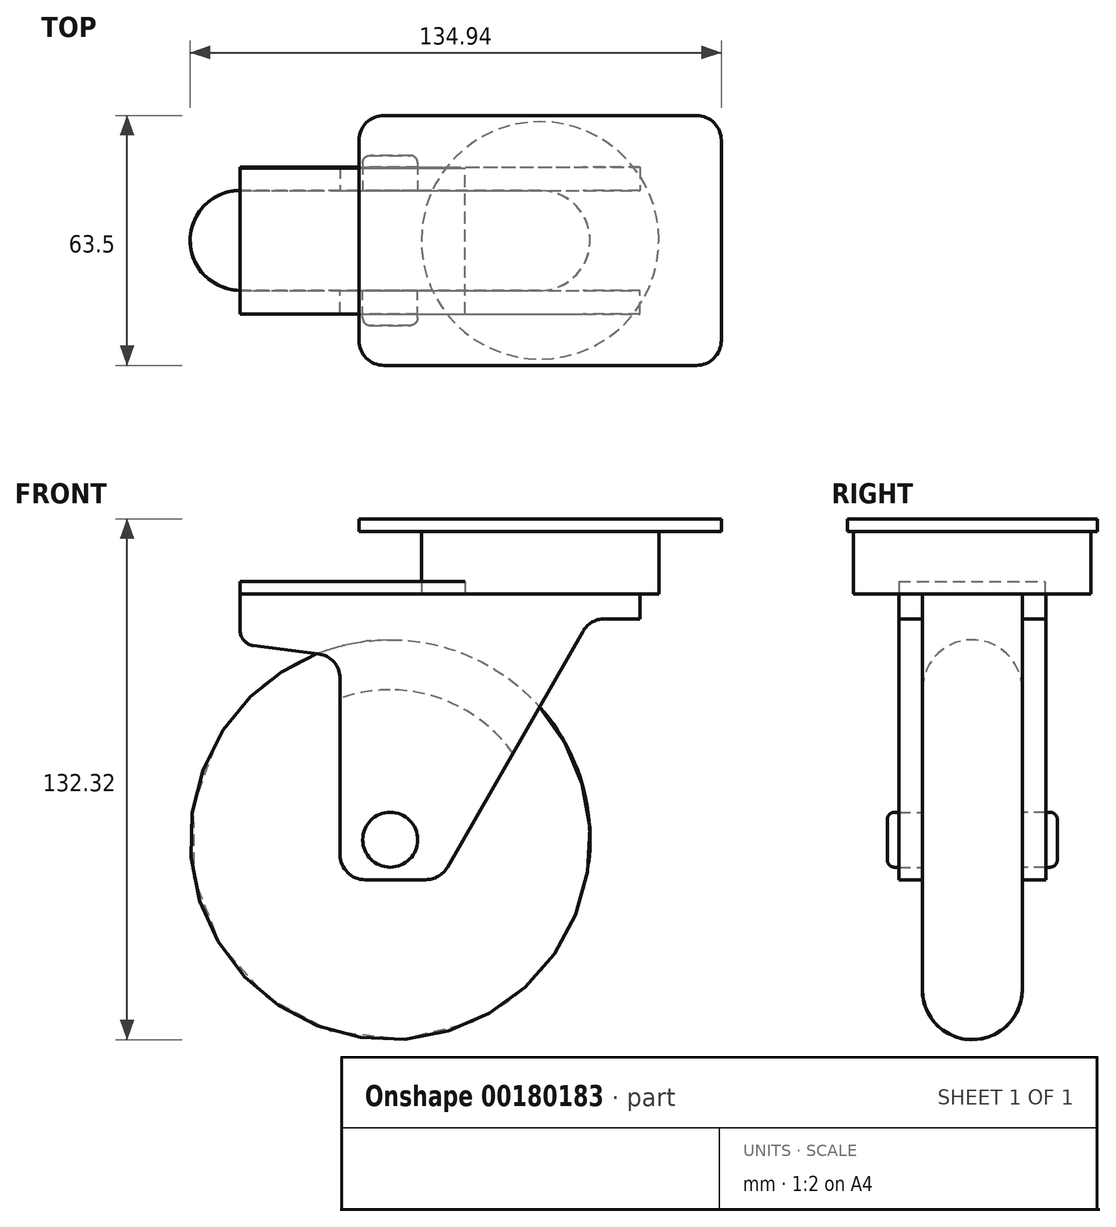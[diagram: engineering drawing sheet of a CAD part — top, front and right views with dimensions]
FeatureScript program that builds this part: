
annotation { "Feature Type Name" : "Feature", "Feature Type Description" : "" }
export const myFeature = defineFeature(function(context is Context, id is Id, definition is map)
    precondition{}
    {
        {
            var Q0;
            Q0=qCreatedBy(makeId("Right.planeOp"),FACE);
            var sketch = newSketch(context, id + "F0", { "sketchPlane" : qUnion([Q0])});
            skLineSegment(sketch, "E0.bottom", {"start": v(0, 0) * mm, "end": v(12.7, 0) * mm});
            skLineSegment(sketch, "E0.top", {"start": v(0, 50.8) * mm, "end": v(0, 50.8) * mm});
            skLineSegment(sketch, "E0.left", {"start": v(0, 0) * mm, "end": v(0, 50.8) * mm});
            skLineSegment(sketch, "E0.right", {"start": v(12.7, 0) * mm, "end": v(12.7, 38.1) * mm});
            skPoint(sketch, "E1.visualSharp", {"position": v(12.7, 50.8) * mm});
            skArc(sketch, "E1.filletArc", {"start": v(12.7, 38.1) * mm, "mid": v(8.98, 47.08) * mm, "end": v(0, 50.8) * mm});
            skLineSegment(sketch, "E2", {"start": v(0, 0) * mm, "end": v(29.52, 0) * mm, "construction": true});
            skPoint(sketch, "E2.endSnap0", {"position": v(6.35, 0) * mm});
            skLineSegment(sketch, "E3.MirrorCS", {"start": v(0, 0) * mm, "end": v(-12.7, 0) * mm});
            skLineSegment(sketch, "E4.MirrorCS", {"start": v(-12.7, 0) * mm, "end": v(-12.7, 38.1) * mm});
            skArc(sketch, "E5.MirrorCS", {"start": v(-12.7, 38.1) * mm, "mid": v(-8.98, 47.08) * mm, "end": v(0, 50.8) * mm});
            skLineSegment(sketch, "E6.MirrorCS", {"start": v(0, 0) * mm, "end": v(-29.52, 0) * mm, "construction": true});
            skSolve(sketch);
        }
        {
            var Q0;
            Q0=makeQuery(id+"F0.imprint","IMPRINT",FACE,{"disambiguationData":[TD([[makeQuery(id+"F0.imprint","IMPRINT",EDGE,{"derivedFrom":sQuery(id+"F0.wireOp",EDGE,"E0.left")}),1.0]])]});
            var Q1;
            Q1=makeQuery(id+"F0.imprint","IMPRINT",FACE,{"disambiguationData":[TD([[makeQuery(id+"F0.imprint","IMPRINT",EDGE,{"derivedFrom":sQuery(id+"F0.wireOp",EDGE,"E0.bottom")}),1.0]])]});
            var Q2;
            Q2=sQuery(id+"F0.wireOp",EDGE,"E6.MirrorCS");
            revolve(context, id + "F1", {"entities" : qUnion([Q0, Q1]), "axis" : qUnion([Q2]), "revolveType" : RevolveType.FULL});
        }
        {
            var Q0;
            Q0=makeQuery(id+"F1.opRevolve","SWEPT_FACE",FACE,{"disambiguationData":[OSD([sQuery(id+"F0.wireOp",EDGE,"E4.MirrorCS")])]});
            var sketch = newSketch(context, id + "F2", { "sketchPlane" : qUnion([Q0])});
            skCircle(sketch, "E7", {"center": v(0, 0) * mm, "radius": 6.99 * mm});
            skSolve(sketch);
        }
        {
            var Q0;
            Q0=qSketchRegion(id+"F2",true);
            extrude(context, id + "F3", {"entities" : qUnion([Q0]), "operationType" : NewBodyOperationType.ADD, "depth" : 8.9 * mm});
        }
        {
            var Q0;
            Q0=makeQuery(id+"F3.opExtrude","CAP_EDGE",EDGE,{"disambiguationData":[OSD([sQuery(id+"F2.wireOp",EDGE,"E7")])],"isStart":false});
            fillet(context, id + "F4", {"entities" : qUnion([Q0]), "radius" : 1.96 * mm, "tangentPropagation" : true, "allowEdgeOverflow" : false});
        }
        {
            var Q0;
            Q0=makeQuery(id+"F1.opRevolve","SWEPT_FACE",FACE,{"disambiguationData":[OSD([sQuery(id+"F0.wireOp",EDGE,"E0.right")])]});
            var sketch = newSketch(context, id + "F5", { "sketchPlane" : qUnion([Q0])});
            skCircle(sketch, "E8", {"center": v(0, 0) * mm, "radius": 6.99 * mm});
            skSolve(sketch);
        }
        {
            var Q0;
            Q0=qSketchRegion(id+"F5",true);
            extrude(context, id + "F6", {"entities" : qUnion([Q0]), "operationType" : NewBodyOperationType.ADD, "depth" : 8.9 * mm});
        }
        {
            var Q0;
            Q0=makeQuery(id+"F6.opExtrude","CAP_FACE",FACE,{"disambiguationData":[OSD([sQuery(id+"F5.wireOp",EDGE,"E8")])],"isStart":false});
            fillet(context, id + "F7", {"entities" : qUnion([Q0]), "radius" : 1.84 * mm, "tangentPropagation" : true, "allowEdgeOverflow" : false});
        }
        {
            var Q0;
            Q0=makeQuery(id+"F1.opRevolve","SWEPT_FACE",FACE,{"disambiguationData":[OSD([sQuery(id+"F0.wireOp",EDGE,"E4.MirrorCS")])]});
            var sketch = newSketch(context, id + "F8", { "sketchPlane" : qUnion([Q0])});
            skLineSegment(sketch, "E9.top", {"start": v(0, 62.47) * mm, "end": v(12.7, 62.47) * mm});
            skLineSegment(sketch, "E9.left", {"start": v(0, 0) * mm, "end": v(0, 62.47) * mm, "construction": true});
            skLineSegment(sketch, "E9.right", {"start": v(12.7, 0) * mm, "end": v(12.7, 62.47) * mm});
            skLineSegment(sketch, "E10.top", {"start": v(1.75, 62.47) * mm, "end": v(-12.7, 62.47) * mm});
            skLineSegment(sketch, "E10.right", {"start": v(-12.7, 0) * mm, "end": v(-12.7, 40.93) * mm});
            skLineSegment(sketch, "E11.top", {"start": v(-6.35, -10.16) * mm, "end": v(9.03, -10.16) * mm});
            skLineSegment(sketch, "E11.left", {"start": v(-12.7, 0) * mm, "end": v(-12.7, -3.81) * mm});
            skLineSegment(sketch, "E11.right", {"start": v(12.7, 0) * mm, "end": v(12.7, -10.16) * mm});
            skPoint(sketch, "E12.visualSharp", {"position": v(-12.7, -10.16) * mm});
            skArc(sketch, "E12.filletArc", {"start": v(-12.7, -3.81) * mm, "mid": v(-10.84, -8.3) * mm, "end": v(-6.35, -10.16) * mm});
            skLineSegment(sketch, "E13", {"start": v(0, 62.47) * mm, "end": v(-38.1, 62.47) * mm});
            skLineSegment(sketch, "E14", {"start": v(-38.1, 62.47) * mm, "end": v(-38.1, 53.12) * mm});
            skLineSegment(sketch, "E15", {"start": v(-34.77, 49.34) * mm, "end": v(-18.24, 47.23) * mm});
            skLineSegment(sketch, "E16", {"start": v(12.7, 62.47) * mm, "end": v(63.5, 62.47) * mm});
            skLineSegment(sketch, "E17", {"start": v(63.5, 62.47) * mm, "end": v(63.5, 56.12) * mm});
            skLineSegment(sketch, "E18", {"start": v(63.5, 56.12) * mm, "end": v(54.47, 56.12) * mm});
            skLineSegment(sketch, "E19", {"start": v(14.53, -6.97) * mm, "end": v(48.97, 52.94) * mm});
            skPoint(sketch, "E20.visualSharp", {"position": v(12.7, -10.16) * mm});
            skArc(sketch, "E20.filletArc", {"start": v(9.03, -10.16) * mm, "mid": v(12.2, -9.3) * mm, "end": v(14.53, -6.97) * mm});
            skArc(sketch, "E21.filletArc", {"start": v(-12.7, 40.93) * mm, "mid": v(-14.28, 45.13) * mm, "end": v(-18.24, 47.23) * mm});
            skPoint(sketch, "E22.visualSharp", {"position": v(-38.1, 49.77) * mm});
            skArc(sketch, "E22.filletArc", {"start": v(-38.1, 53.12) * mm, "mid": v(-37.15, 50.6) * mm, "end": v(-34.77, 49.34) * mm});
            skPoint(sketch, "E23.visualSharp", {"position": v(50.8, 56.12) * mm});
            skArc(sketch, "E23.filletArc", {"start": v(54.47, 56.12) * mm, "mid": v(51.3, 55.27) * mm, "end": v(48.97, 52.94) * mm});
            skSolve(sketch);
        }
        {
            var Q0;
            Q0=qSketchRegion(id+"F8",true);
            extrude(context, id + "F9", {"entities" : qUnion([Q0]), "operationType" : NewBodyOperationType.ADD, "depth" : 5.97 * mm});
        }
        {
            var Q0;
            Q0=makeQuery(id+"F1.opRevolve","SWEPT_BODY",BODY,{"disambiguationData":[OSD([sQuery(id+"F0.wireOp",EDGE,"E0.bottom"),sQuery(id+"F0.wireOp",EDGE,"E0.right"),sQuery(id+"F0.wireOp",EDGE,"E1.filletArc"),sQuery(id+"F0.wireOp",EDGE,"E3.MirrorCS"),sQuery(id+"F0.wireOp",EDGE,"E4.MirrorCS"),sQuery(id+"F0.wireOp",EDGE,"E5.MirrorCS")])]});
            var Q1;
            Q1=qCreatedBy(makeId("Front.planeOp"),FACE);
            mirror(context, id + "F10", {"entities" : qUnion([Q0]), "mirrorPlane" : qUnion([Q1])});
        }
        {
            var Q0;
            Q0=makeQuery(id+"F9.opExtrude","SWEPT_FACE",FACE,{"disambiguationData":[OSD([sQuery(id+"F8.wireOp",EDGE,"E9.top"),sQuery(id+"F8.wireOp",EDGE,"E10.top"),sQuery(id+"F8.wireOp",EDGE,"E13"),sQuery(id+"F8.wireOp",EDGE,"E16")])]});
            var sketch = newSketch(context, id + "F11", { "sketchPlane" : qUnion([Q0])});
            skLineSegment(sketch, "E24", {"start": v(0, 0) * mm, "end": v(38.1, 0) * mm, "construction": true});
            skCircle(sketch, "E25", {"center": v(38.1, 0) * mm, "radius": 30.16 * mm});
            skSolve(sketch);
        }
        {
            var Q0;
            {var subQ0=sQuery(id+"F11.wireOp",EDGE,"E25");var subQ1=sQuery(id+"F8.wireOp",EDGE,"E16");var subQ4=makeQuery(id+"F9.opExtrude","SWEPT_EDGE",EDGE,{"disambiguationData":[OSD([subQ1,sQuery(id+"F8.wireOp",EDGE,"E17")])]});var subQ5=makeQuery(id+"F11.imprint","INTERSECT",VERTEX,{"derivedFrom":[subQ4,subQ0]});Q0=makeQuery(id+"F11.imprint","IMPRINT",FACE,{"disambiguationData":[TD([[makeQuery(id+"F11.imprint","IMPRINT",EDGE,{"disambiguationData":[TD([[subQ5,-1.0]])],"derivedFrom":subQ0}),1.0]])]});}
            var Q1;
            {var subQ0=sQuery(id+"F8.wireOp",EDGE,"E16");var subQ5=makeQuery(id+"F9.opExtrude","SWEPT_EDGE",EDGE,{"disambiguationData":[OSD([subQ0,sQuery(id+"F8.wireOp",EDGE,"E17")])]});var subQ7=sQuery(id+"F11.wireOp",EDGE,"E25");var subQ9=makeQuery(id+"F11.imprint","INTERSECT",VERTEX,{"derivedFrom":[subQ5,subQ7]});Q1=makeQuery(id+"F11.imprint","IMPRINT",FACE,{"disambiguationData":[TD([[makeQuery(id+"F11.imprint","IMPRINT",EDGE,{"disambiguationData":[TD([[subQ9,1.0]])],"derivedFrom":subQ7}),1.0]])]});}
            var Q2;
            {var subQ0=sQuery(id+"F11.wireOp",EDGE,"E25");var subQ1=makeQuery(id+"F9.opExtrude","CAP_EDGE",EDGE,{"disambiguationData":[OSD([sQuery(id+"F8.wireOp",EDGE,"E9.top"),sQuery(id+"F8.wireOp",EDGE,"E10.top"),sQuery(id+"F8.wireOp",EDGE,"E13"),sQuery(id+"F8.wireOp",EDGE,"E16")])],"isStart":false});var subQ2=makeQuery(id+"F11.imprint","INTERSECT",VERTEX,{"disambiguationData":[OD(0.0)],"derivedFrom":[subQ1,subQ0]});Q2=makeQuery(id+"F11.imprint","IMPRINT",FACE,{"disambiguationData":[TD([[makeQuery(id+"F11.imprint","IMPRINT",EDGE,{"disambiguationData":[TD([[subQ2,-1.0]])],"derivedFrom":subQ0}),1.0]])]});}
            var Q3;
            Q3=sQuery(id+"F11.wireOp",EDGE,"E25");
            extrude(context, id + "F12", {"entities" : qUnion([Q0, Q1, Q2]), "surfaceEntities" : qUnion([Q3]), "depth" : 19.05 * mm});
        }
        {
            var Q0;
            Q0=makeQuery(id+"F12.opExtrude","CAP_FACE",FACE,{"disambiguationData":[OSD([sQuery(id+"F11.wireOp",EDGE,"E25")])],"isStart":false});
            var sketch = newSketch(context, id + "F13", { "sketchPlane" : qUnion([Q0])});
            skLineSegment(sketch, "E26.bottom", {"start": v(77.79, -31.75) * mm, "end": v(-1.59, -31.75) * mm});
            skLineSegment(sketch, "E26.top", {"start": v(77.79, 31.75) * mm, "end": v(-1.59, 31.75) * mm});
            skLineSegment(sketch, "E26.left", {"start": v(84.14, -25.4) * mm, "end": v(84.14, 25.4) * mm});
            skLineSegment(sketch, "E26.right", {"start": v(-7.94, -25.4) * mm, "end": v(-7.94, 25.4) * mm});
            skPoint(sketch, "E26.middle", {"position": v(38.1, 0) * mm});
            skPoint(sketch, "E27.visualSharp", {"position": v(84.14, 31.75) * mm});
            skArc(sketch, "E27.filletArc", {"start": v(84.14, 25.4) * mm, "mid": v(82.28, 29.9) * mm, "end": v(77.79, 31.75) * mm});
            skPoint(sketch, "E28.visualSharp", {"position": v(84.14, -31.75) * mm});
            skArc(sketch, "E28.filletArc", {"start": v(77.79, -31.75) * mm, "mid": v(82.28, -29.9) * mm, "end": v(84.14, -25.4) * mm});
            skPoint(sketch, "E29.visualSharp", {"position": v(-7.94, -31.75) * mm});
            skArc(sketch, "E29.filletArc", {"start": v(-7.94, -25.4) * mm, "mid": v(-6.08, -29.9) * mm, "end": v(-1.59, -31.75) * mm});
            skPoint(sketch, "E30.visualSharp", {"position": v(-7.94, 31.75) * mm});
            skArc(sketch, "E30.filletArc", {"start": v(-1.59, 31.75) * mm, "mid": v(-6.08, 29.9) * mm, "end": v(-7.94, 25.4) * mm});
            skSolve(sketch);
        }
        {
            var Q0;
            Q0=qSketchRegion(id+"F13",true);
            extrude(context, id + "F14", {"entities" : qUnion([Q0]), "operationType" : NewBodyOperationType.ADD, "oppositeDirection" : true, "depth" : 3.17 * mm});
        }
        {
            var Q0;
            Q0=makeQuery(id+"F9.opExtrude","SWEPT_FACE",FACE,{"disambiguationData":[OSD([sQuery(id+"F8.wireOp",EDGE,"E9.top"),sQuery(id+"F8.wireOp",EDGE,"E10.top"),sQuery(id+"F8.wireOp",EDGE,"E13"),sQuery(id+"F8.wireOp",EDGE,"E16")])]});
            var sketch = newSketch(context, id + "F15", { "sketchPlane" : qUnion([Q0])});
            skLineSegment(sketch, "E31.bottom", {"start": v(-38.1, -18.67) * mm, "end": v(19.05, -18.67) * mm});
            skLineSegment(sketch, "E31.top", {"start": v(-38.1, 18.42) * mm, "end": v(19.05, 18.42) * mm});
            skLineSegment(sketch, "E31.left", {"start": v(-38.1, -18.67) * mm, "end": v(-38.1, 18.42) * mm});
            skLineSegment(sketch, "E31.right", {"start": v(19.05, -18.67) * mm, "end": v(19.05, 18.42) * mm});
            skSolve(sketch);
        }
        {
            var Q0;
            Q0=qSketchRegion(id+"F15",true);
            extrude(context, id + "F16", {"entities" : qUnion([Q0]), "depth" : 3.17 * mm});
        }
        {
            var Q0;
            Q0=makeQuery(id+"F1.opRevolve","SWEPT_BODY",BODY,{"disambiguationData":[OSD([sQuery(id+"F0.wireOp",EDGE,"E0.bottom"),sQuery(id+"F0.wireOp",EDGE,"E0.right"),sQuery(id+"F0.wireOp",EDGE,"E1.filletArc"),sQuery(id+"F0.wireOp",EDGE,"E3.MirrorCS"),sQuery(id+"F0.wireOp",EDGE,"E4.MirrorCS"),sQuery(id+"F0.wireOp",EDGE,"E5.MirrorCS")])]});
            transform(context, id + "F17", {"entities" : qUnion([Q0]), "transformType" : TransformType.TRANSLATION_3D, "dx" : 0 * mm, "dy" : 0 * mm, "dz" : 0 * mm, "makeCopy" : true});
        }
    });
